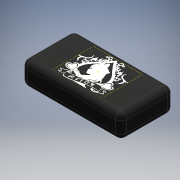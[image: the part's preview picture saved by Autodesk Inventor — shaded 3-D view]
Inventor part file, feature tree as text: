
AUTODESK INVENTOR PART (.ipt)
format: ipt  version: 2016 (Build 200138000, 138)  size: 278,528 bytes
history: native  units: mm
features: other x3, sketch x3, extrude x1, fillet x1
ambient origin geometry x8: Origin, YZ Plane, XZ Plane, XY Plane, X Axis, Y Axis, Z Axis, Center Point
bodies: Body1 (feature_tree)
feature tree (8):
  other  "ソリッド2"
  extrude  "押し出し1"  Depth=34.0mm
  fillet  "フィレット1"  Radius=18.0mm
  sketch  "スケッチ3"
  sketch  "スケッチ4"
  sketch  "スケッチ2"
  other  "イメージ1"
  other  "イメージ2"
